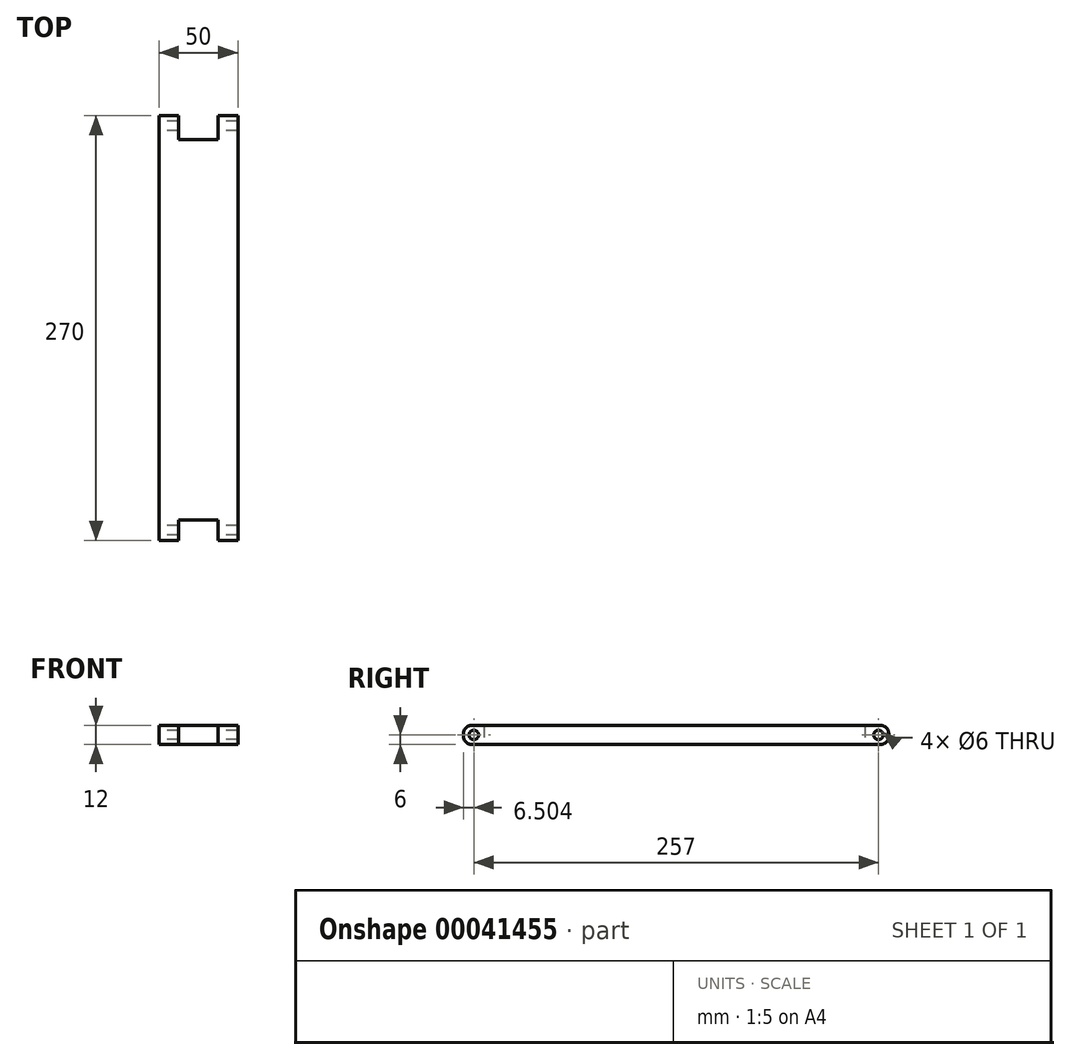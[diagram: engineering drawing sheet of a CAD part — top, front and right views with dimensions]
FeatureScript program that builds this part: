
annotation { "Feature Type Name" : "Feature", "Feature Type Description" : "" }
export const myFeature = defineFeature(function(context is Context, id is Id, definition is map)
    precondition{}
    {
        {
            var Q0;
            Q0=qCreatedBy(makeId("Top.planeOp"),FACE);
            var sketch = newSketch(context, id + "F0", { "sketchPlane" : qUnion([Q0])});
            skLineSegment(sketch, "E0.bottom", {"start": v(-30.03, 97.7) * mm, "end": v(-17.53, 97.7) * mm});
            skLineSegment(sketch, "E0.top", {"start": v(-30.03, -172.3) * mm, "end": v(-17.53, -172.3) * mm});
            skLineSegment(sketch, "E0.left", {"start": v(-30.03, 97.7) * mm, "end": v(-30.03, -172.3) * mm});
            skLineSegment(sketch, "E0.right", {"start": v(19.97, 97.7) * mm, "end": v(19.97, -172.3) * mm});
            skLineSegment(sketch, "E1.top", {"start": v(-17.53, 82.48) * mm, "end": v(7.47, 82.48) * mm});
            skLineSegment(sketch, "E1.left", {"start": v(-17.53, 97.7) * mm, "end": v(-17.53, 82.48) * mm});
            skLineSegment(sketch, "E1.right", {"start": v(7.47, 97.7) * mm, "end": v(7.47, 82.48) * mm});
            skLineSegment(sketch, "E2.top", {"start": v(-17.53, -159.3) * mm, "end": v(7.47, -159.3) * mm});
            skLineSegment(sketch, "E2.left", {"start": v(-17.53, -172.3) * mm, "end": v(-17.53, -159.3) * mm});
            skLineSegment(sketch, "E2.right", {"start": v(7.47, -172.3) * mm, "end": v(7.47, -159.3) * mm});
            skLineSegment(sketch, "E3.trimOffspring", {"start": v(7.47, 97.7) * mm, "end": v(19.97, 97.7) * mm});
            skLineSegment(sketch, "E4.trimOffspring", {"start": v(7.47, -172.3) * mm, "end": v(19.97, -172.3) * mm});
            skSolve(sketch);
        }
        {
            var Q0;
            Q0 = qSketchRegion(id + "F0", true);
            extrude(context, id + "F1", {"entities" : qUnion([Q0]), "depth" : 12 * mm});
        }
        {
            var Q0;
            Q0=makeQuery(id+"F1.opExtrude","SWEPT_FACE",FACE,{"disambiguationData":[OSD([sQuery(id+"F0.wireOp",EDGE,"E0.left")])]});
            var sketch = newSketch(context, id + "F2", { "sketchPlane" : qUnion([Q0])});
            skLineSegment(sketch, "E5", {"start": v(-97.7, 6) * mm, "end": v(172.3, 6) * mm, "construction": true});
            skCircle(sketch, "E6", {"center": v(-91.2, 6) * mm, "radius": 3 * mm});
            skCircle(sketch, "E7", {"center": v(165.8, 6) * mm, "radius": 3 * mm});
            skSolve(sketch);
        }
        {
            var Q0;
            Q0 = qSketchRegion(id + "F2", true);
            extrude(context, id + "F3", {"entities" : qUnion([Q0]), "operationType" : NewBodyOperationType.REMOVE, "endBound" : BoundingType.THROUGH_ALL, "oppositeDirection" : true, "depth" : 25 * mm});
        }
        {
            var Q0;
            Q0=makeQuery(id+"F1.opExtrude","CAP_EDGE",EDGE,{"disambiguationData":[OSD([sQuery(id+"F0.wireOp",EDGE,"E0.bottom")])],"isStart":false});
            var Q1;
            Q1=makeQuery(id+"F1.opExtrude","CAP_EDGE",EDGE,{"disambiguationData":[OSD([sQuery(id+"F0.wireOp",EDGE,"E0.bottom")])],"isStart":true});
            var Q2;
            Q2=makeQuery(id+"F1.opExtrude","CAP_EDGE",EDGE,{"disambiguationData":[OSD([sQuery(id+"F0.wireOp",EDGE,"E3.trimOffspring")])],"isStart":false});
            var Q3;
            Q3=makeQuery(id+"F1.opExtrude","CAP_EDGE",EDGE,{"disambiguationData":[OSD([sQuery(id+"F0.wireOp",EDGE,"E3.trimOffspring")])],"isStart":true});
            var Q4;
            Q4=makeQuery(id+"F1.opExtrude","CAP_EDGE",EDGE,{"disambiguationData":[OSD([sQuery(id+"F0.wireOp",EDGE,"E0.top")])],"isStart":false});
            var Q5;
            Q5=makeQuery(id+"F1.opExtrude","CAP_EDGE",EDGE,{"disambiguationData":[OSD([sQuery(id+"F0.wireOp",EDGE,"E4.trimOffspring")])],"isStart":false});
            var Q6;
            Q6=makeQuery(id+"F1.opExtrude","CAP_EDGE",EDGE,{"disambiguationData":[OSD([sQuery(id+"F0.wireOp",EDGE,"E0.top")])],"isStart":true});
            var Q7;
            Q7=makeQuery(id+"F1.opExtrude","CAP_EDGE",EDGE,{"disambiguationData":[OSD([sQuery(id+"F0.wireOp",EDGE,"E4.trimOffspring")])],"isStart":true});
            fillet(context, id + "F4", {"entities" : qUnion([Q0, Q1, Q2, Q3, Q4, Q5, Q6, Q7]), "radius" : 5 * mm, "tangentPropagation" : true, "allowEdgeOverflow" : false});
        }
    });
